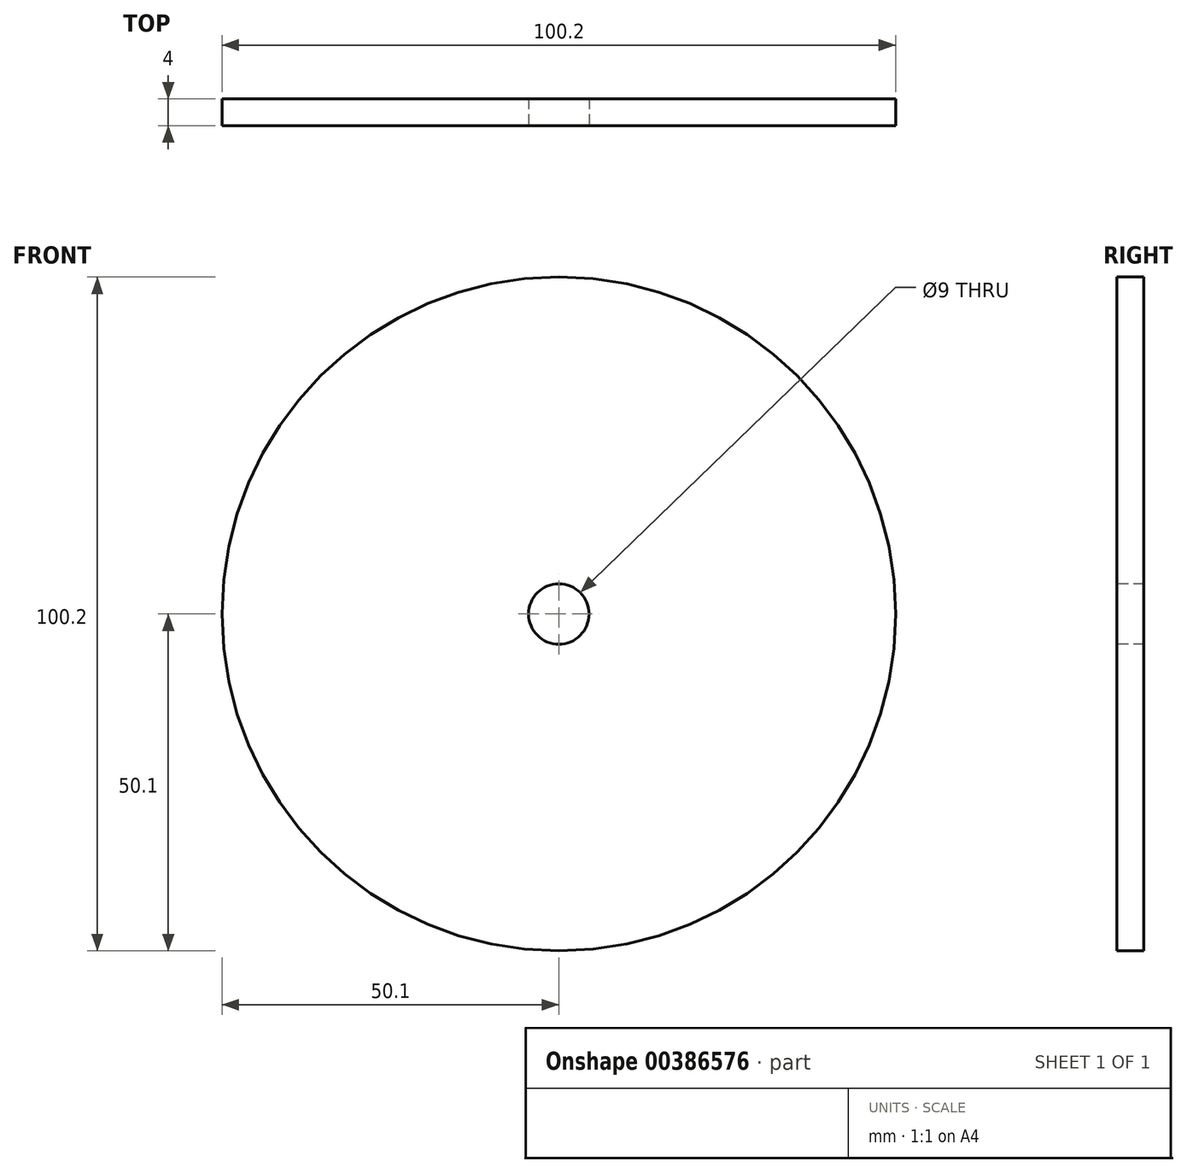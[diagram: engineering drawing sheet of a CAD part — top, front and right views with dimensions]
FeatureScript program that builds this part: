
annotation { "Feature Type Name" : "Feature", "Feature Type Description" : "" }
export const myFeature = defineFeature(function(context is Context, id is Id, definition is map)
    precondition{}
    {
        {
            var Q0;
            Q0=qCreatedBy(makeId("Front.planeOp"),FACE);
            var sketch = newSketch(context, id + "F0", { "sketchPlane" : qUnion([Q0])});
            skCircle(sketch, "E0", {"center": v(0, 0) * mm, "radius": 50.1 * mm});
            skCircle(sketch, "E1", {"center": v(0, 0) * mm, "radius": 4.5 * mm});
            skArc(sketch, "E2", {"start": v(20.8, 23.96) * mm, "mid": v(-0.42, 37.24) * mm, "end": v(-20.8, 22.7) * mm});
            skArc(sketch, "E3", {"start": v(20.8, -20.8) * mm, "mid": v(-0.93, -6.8) * mm, "end": v(-20.8, -23.33) * mm});
            skSolve(sketch);
        }
        {
            var Q0;
            Q0=makeQuery(id+"F0.imprint","IMPRINT",FACE,{"disambiguationData":[TD([[makeQuery(id+"F0.imprint","IMPRINT",EDGE,{"derivedFrom":sQuery(id+"F0.wireOp",EDGE,"E0")}),1.0]])]});
            var Q1;
            Q1=makeQuery(id+"F0.imprint","IMPRINT",FACE,{"disambiguationData":[TD([[makeQuery(id+"F0.imprint","IMPRINT",EDGE,{"derivedFrom":sQuery(id+"F0.wireOp",EDGE,"E1")}),1.0]])]});
            extrude(context, id + "F1", {"entities" : qUnion([Q0, Q1]), "depth" : 3 * mm});
        }
        {
            var Q0;
            Q0 = qSketchRegion(id + "F0", true);
            var Q1;
            Q1=makeQuery(id+"F1.opExtrude","CAP_FACE",FACE,{"disambiguationData":[OSD([sQuery(id+"F0.wireOp",EDGE,"E0")])],"isStart":false});
            extrude(context, id + "F2", {"entities" : qUnion([Q0, Q1]), "operationType" : NewBodyOperationType.ADD, "oppositeDirection" : true, "depth" : 1 * mm});
        }
        {
            var Q0;
            Q0=makeQuery(id+"F1.opExtrude","CAP_FACE",FACE,{"disambiguationData":[OSD([sQuery(id+"F0.wireOp",EDGE,"E0")])],"isStart":false});
            var sketch = newSketch(context, id + "F3", { "sketchPlane" : qUnion([Q0])});
            skCircle(sketch, "E4", {"center": v(0, 0) * mm, "radius": 4.5 * mm});
            skSolve(sketch);
        }
        {
            var Q0;
            Q0 = qSketchRegion(id + "F3", true);
            extrude(context, id + "F4", {"entities" : qUnion([Q0]), "operationType" : NewBodyOperationType.REMOVE, "oppositeDirection" : true, "depth" : 25 * mm});
        }
    });
